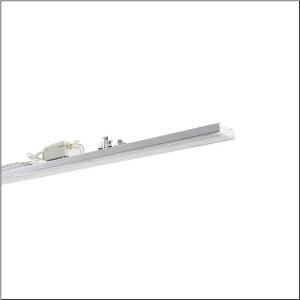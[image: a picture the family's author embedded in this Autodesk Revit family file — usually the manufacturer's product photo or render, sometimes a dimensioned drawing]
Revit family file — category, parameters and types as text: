
# Revit family: licross_r__21_recessed_ho_52te12mn4fxm_584e
name_source: partatom
category: Lighting Fixtures
units: mm (PartAtom-declared; Revit-internal decimal feet)

## family parameters
Cut with Voids When Loaded = No
Host = Face
Light Source = No
Part Type = Normal
Room Calculation Point = No
Round Connector Dimension = Use Diameter
Shared = No

## types (1)
- --- (1 x LED, 15100 lm, 83.1 W, 4000K)
    Apparent Load = 83 VA
    CIE Flux Codes = 69 91 98 100 100
    Color Rendering = 80
    Color Temperature = 4000K
    Default Elevation = 1800 mm
    Description = Licross® 21 Recessed HO, luminaire insert, of sheet steel, galvanised, coil coated, white, length: 1.500mm, width: 66mm, height: 67mm, LED rated luminous flux: 15.100lm, light colour: 840, control gear: ON/OFF Multilumen, with plug, 3-pole, with phase selection, mains connection: 220..240V, AC, 50/60Hz, rated input power: 83W, halogen-free wiring, primary optical cover: cover, of PMMA, light emission: direct distribution, primary light characteristic: symmetric, protection rating (complete): IP54, insulation class (complete): insulation class I (protective earthing), certification: CE, ENEC, VDE, UKCA, protection symbol: D if used in an environment with non-conductive dust loads with corresponding accessories, impact resistance: IK06, permissible ambient temperature for indoor applications: -35..+30°C, corresponds to IFS (International Featured Standards) requirements for safety and quality in the food industry, reducing of maximum allowable ambient temperature of 5°C with ceiling mounting, LABS conformity tested according to VDMA 24364:2018-05, packaging unit: 1 piece
    Height = 58 mm
    Lamp = 1 x LED
    Lamp Light Flux = 15100 lm
    Lamp Power = 83.1 W
    Lamp count = 1
    Length = 1500 mm
    Luminous efficacy = 182 lm/W
    Manufacturer = Siteco
    ModVariant = No
    Model = 52TE12MN4FXM
    Mounting Place = Ceiling
    Mounting Type = Pendant
    Number of Poles = 1
    OnlyDefault = Yes
    Power Factor = 1
    Product Name = Licross® 21 Recessed HO
    Product group = luminaire insert
    ProductGroupID = 901
    Protection Class = Protection class I
    Protection Degree = IP 54
    RLX_Detail_Level = 1
    RLX_Emergency_Light_Flux = 0 lm
    RLX_Emergency_Type = 0
    RLX_Emergency_Type_DB = No
    RlxData = <blob elided: 22385 chars, md5=bc8ec0e3>
    Socket = socket
    Standby Power = 0 W
    System Light Flux = 15100 lm
    System Power = 83 W
    Type Comments = factory setting: luminous flux: 100 % | (A | C | E) | 195 mA
    Type Image = l_1296930.jpg
    URL = http://relux.com
    VarID = @adj_033279
    Voltage = 0 V
    Weight = 0.00 kg
    Width = 66 mm

## geometry (parser evidence)
native form markers: Blend x4, Sweep x9
no freeform markers — native parametric forms only
